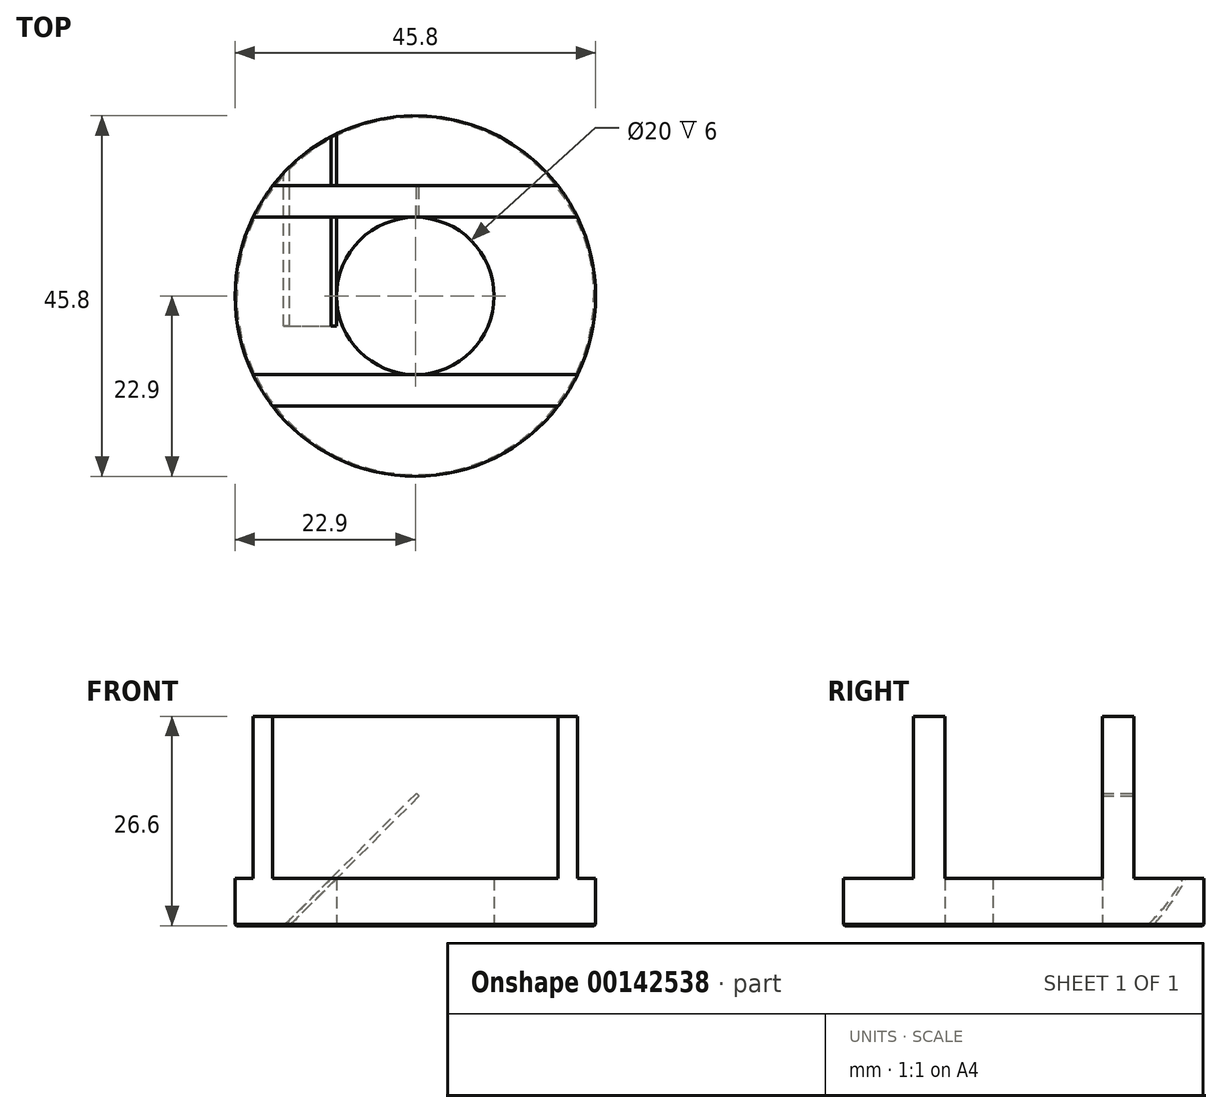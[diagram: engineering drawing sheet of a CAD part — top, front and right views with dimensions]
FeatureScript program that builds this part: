
annotation { "Feature Type Name" : "Feature", "Feature Type Description" : "" }
export const myFeature = defineFeature(function(context is Context, id is Id, definition is map)
    precondition{}
    {
        {
            var Q0;
            Q0=qCreatedBy(makeId("Top.planeOp"),FACE);
            var sketch = newSketch(context, id + "F0", { "sketchPlane" : qUnion([Q0])});
            skCircle(sketch, "E0", {"center": v(0, 0) * mm, "radius": 22.9 * mm});
            skLineSegment(sketch, "E1", {"start": v(-18.12, 14) * mm, "end": v(18.12, 14) * mm});
            skLineSegment(sketch, "E2", {"start": v(-20.6, 10) * mm, "end": v(20.6, 10) * mm});
            skLineSegment(sketch, "E3.MirrorCS", {"start": v(-18.12, -14) * mm, "end": v(18.12, -14) * mm});
            skLineSegment(sketch, "E4.MirrorCS", {"start": v(-20.6, -10) * mm, "end": v(20.6, -10) * mm});
            skLineSegment(sketch, "E5", {"start": v(-16, 10) * mm, "end": v(-16, -10) * mm});
            skCircle(sketch, "E6", {"center": v(0, 0) * mm, "radius": 10 * mm});
            skSolve(sketch);
        }
        {
            var Q0;
            Q0 = qSketchRegion(id + "F0", true);
            var Q1;
            {var subQ0=sQuery(id+"F0.wireOp",EDGE,"E5");var subQ1=sQuery(id+"F0.wireOp",EDGE,"E4.MirrorCS");var subQ2=makeQuery(id+"F0.imprint","INTERSECT",VERTEX,{"derivedFrom":[subQ1,subQ0]});Q1=makeQuery(id+"F0.imprint","IMPRINT",FACE,{"disambiguationData":[TD([[makeQuery(id+"F0.imprint","IMPRINT",EDGE,{"disambiguationData":[TD([[subQ2,-1.0]])],"derivedFrom":subQ1}),1.0]])]});}
            var Q2;
            {var subQ0=sQuery(id+"F0.wireOp",EDGE,"E5");var subQ1=sQuery(id+"F0.wireOp",EDGE,"E2");var subQ2=makeQuery(id+"F0.imprint","INTERSECT",VERTEX,{"derivedFrom":[subQ1,subQ0]});Q2=makeQuery(id+"F0.imprint","IMPRINT",FACE,{"disambiguationData":[TD([[makeQuery(id+"F0.imprint","IMPRINT",EDGE,{"disambiguationData":[TD([[subQ2,-1.0]])],"derivedFrom":subQ1}),-1.0]])]});}
            extrude(context, id + "F1", {"entities" : qUnion([Q0, Q1, Q2]), "depth" : 6 * mm});
        }
        {
            var Q0;
            {var subQ0=sQuery(id+"F0.wireOp",EDGE,"E1");Q0=makeQuery(id+"F0.imprint","IMPRINT",FACE,{"disambiguationData":[TD([[makeQuery(id+"F0.imprint","IMPRINT",EDGE,{"derivedFrom":subQ0}),-1.0]])]});}
            var Q1;
            {var subQ0=sQuery(id+"F0.wireOp",EDGE,"E3.MirrorCS");Q1=makeQuery(id+"F0.imprint","IMPRINT",FACE,{"disambiguationData":[TD([[makeQuery(id+"F0.imprint","IMPRINT",EDGE,{"derivedFrom":subQ0}),1.0]])]});}
            var Q2;
            Q2 = qSketchRegion(id + "F4", true);
            extrude(context, id + "F2", {"entities" : qUnion([Q0, Q1, Q2]), "operationType" : NewBodyOperationType.ADD, "depth" : 26.6 * mm});
        }
        {
            var Q0;
            Q0=sQuery(id+"F0.wireOp",EDGE,"E5");
            cPlane(context, id + "F3", {"entities" : qUnion([Q0]), "cplaneType" : CPlaneType.LINE_ANGLE, "offset" : 25 * mm, "angle" : 45 * degree, "width" : 150 * mm, "height" : 150 * mm});
        }
        {
            var Q0;
            Q0=qCreatedBy(id+"F3.planeOp",FACE);
            var sketch = newSketch(context, id + "F4", { "sketchPlane" : qUnion([Q0])});
            skLineSegment(sketch, "E7", {"start": v(-2.83, -10) * mm, "end": v(-2.83, 10) * mm});
            skLineSegment(sketch, "E8", {"start": v(26.3, -14) * mm, "end": v(26.3, -10) * mm});
            skLineSegment(sketch, "E9", {"start": v(26.3, 10) * mm, "end": v(26.3, 14) * mm});
            skLineSegment(sketch, "E10.left", {"start": v(-2.83, -12) * mm, "end": v(-2.83, 12) * mm});
            skLineSegment(sketch, "E10.right", {"start": v(26.3, -12) * mm, "end": v(26.3, 12) * mm});
            skLineSegment(sketch, "E11.bottom", {"start": v(-3.83, -12) * mm, "end": v(28.3, -12) * mm});
            skLineSegment(sketch, "E11.top", {"start": v(-3.83, 12) * mm, "end": v(28.3, 12) * mm});
            skLineSegment(sketch, "E11.left", {"start": v(-3.83, -12) * mm, "end": v(-3.83, 12) * mm});
            skLineSegment(sketch, "E11.right", {"start": v(28.3, -12) * mm, "end": v(28.3, 12) * mm});
            skSolve(sketch);
        }
        {
            var Q0;
            {var subQ1=sQuery(id+"F4.wireOp",EDGE,"E7");Q0=makeQuery(id+"F4.imprint","IMPRINT",FACE,{"disambiguationData":[TD([[makeQuery(id+"F4.imprint","IMPRINT",EDGE,{"derivedFrom":subQ1}),1.0]])]});}
            var Q1;
            {var subQ1=sQuery(id+"F4.wireOp",EDGE,"E7");Q1=makeQuery(id+"F4.imprint","IMPRINT",FACE,{"disambiguationData":[TD([[makeQuery(id+"F4.imprint","IMPRINT",EDGE,{"derivedFrom":subQ1}),-1.0]])]});}
            var Q2;
            {var subQ0=sQuery(id+"F4.wireOp",EDGE,"E10.right");Q2=makeQuery(id+"F4.imprint","IMPRINT",FACE,{"disambiguationData":[TD([[makeQuery(id+"F4.imprint","IMPRINT",EDGE,{"derivedFrom":subQ0}),-1.0]])]});}
            extrude(context, id + "F5", {"entities" : qUnion([Q0, Q1, Q2]), "oppositeDirection" : true, "depth" : 0.5 * mm});
        }
        {
            var Q0;
            Q0=makeQuery(id+"F5.opExtrude","SWEPT_BODY",BODY,{"disambiguationData":[OSD([sQuery(id+"F4.wireOp",EDGE,"E11.bottom"),sQuery(id+"F4.wireOp",EDGE,"E11.top"),sQuery(id+"F4.wireOp",EDGE,"E11.left"),sQuery(id+"F4.wireOp",EDGE,"E11.right")])]});
            var Q1;
            Q1=makeQuery(id+"F1.opExtrude","SWEPT_BODY",BODY,{"disambiguationData":[OSD([sQuery(id+"F0.wireOp",EDGE,"E0")])]});
            booleanBodies(context, id + "F6", {"operationType" : BooleanOperationType.SUBTRACTION, "tools" : qUnion([Q0]), "targets" : qUnion([Q1])});
        }
        {
            var Q0;
            Q0=makeQuery(id+"F1.opExtrude","CAP_EDGE",EDGE,{"disambiguationData":[OSD([sQuery(id+"F0.wireOp",EDGE,"E0")])],"isStart":true});
            chamfer(context, id + "F7", {"entities" : qUnion([Q0]), "width" : 0.2 * mm, "tangentPropagation" : true});
        }
    });
